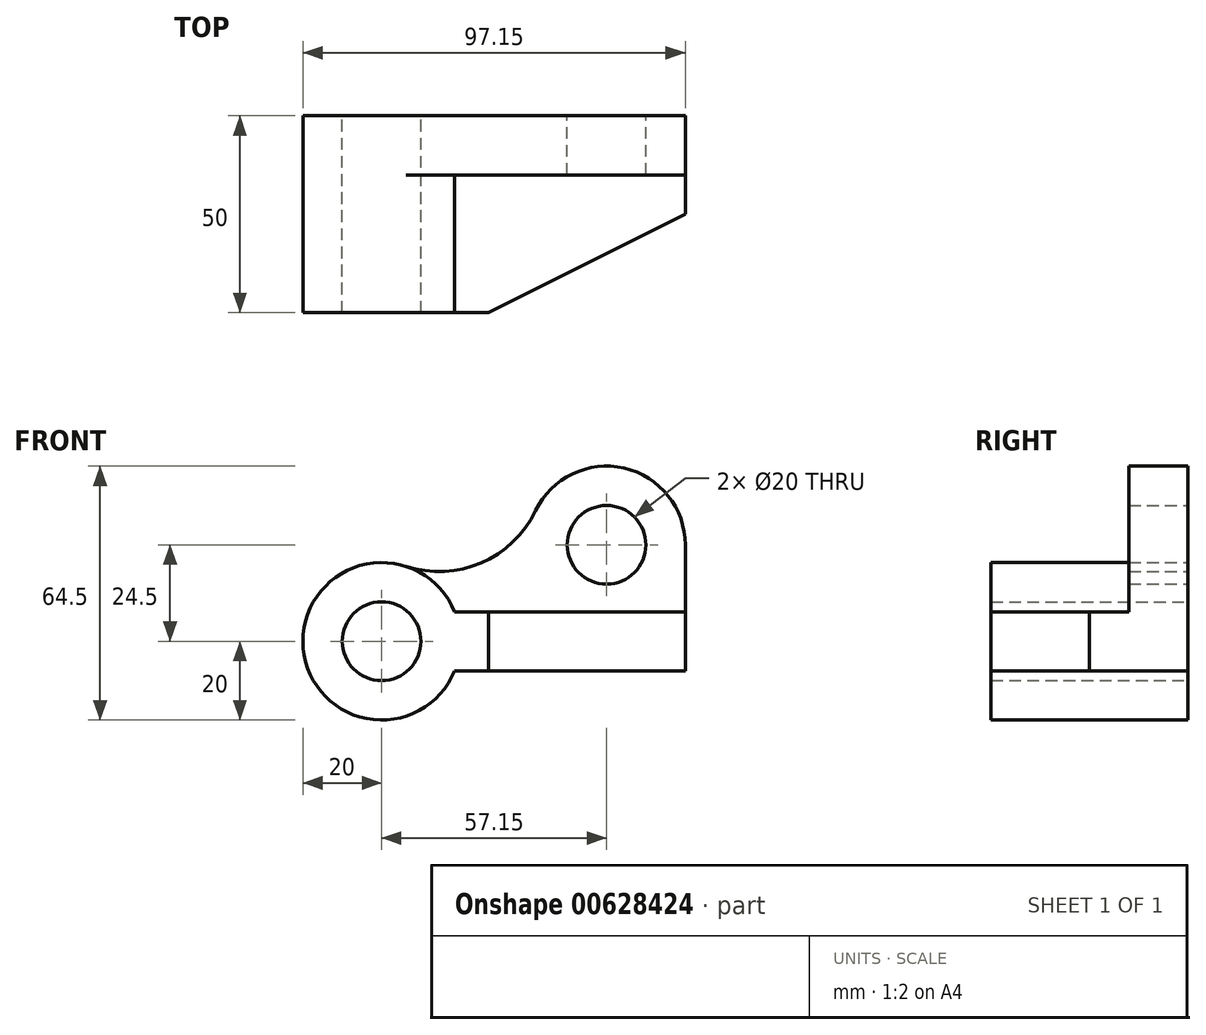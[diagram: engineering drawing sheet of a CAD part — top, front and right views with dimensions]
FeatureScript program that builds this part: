
annotation { "Feature Type Name" : "Feature", "Feature Type Description" : "" }
export const myFeature = defineFeature(function(context is Context, id is Id, definition is map)
    precondition{}
    {
        {
            var Q0;
            Q0=qCreatedBy(makeId("Front.planeOp"),FACE);
            var sketch = newSketch(context, id + "F0", { "sketchPlane" : qUnion([Q0])});
            skLineSegment(sketch, "E0", {"start": v(13.94, 14.34) * mm, "end": v(13.94, 14.34) * mm});
            skCircle(sketch, "E1", {"center": v(0, 0) * mm, "radius": 10 * mm});
            skArc(sketch, "E2", {"start": v(77.15, 24.5) * mm, "mid": v(61.6, 44) * mm, "end": v(39.13, 33.17) * mm});
            skPoint(sketch, "E3.third.point", {"position": v(14.66, 74.72) * mm});
            skCircle(sketch, "E4", {"center": v(0, 0) * mm, "radius": 20 * mm});
            skLineSegment(sketch, "E5.bottom", {"start": v(77.15, 7.5) * mm, "end": v(18.54, 7.5) * mm});
            skLineSegment(sketch, "E5.top", {"start": v(77.15, -7.5) * mm, "end": v(18.54, -7.5) * mm});
            skLineSegment(sketch, "E5.left", {"start": v(77.15, 7.5) * mm, "end": v(77.15, -7.5) * mm});
            skPoint(sketch, "E5.middle", {"position": v(45.2, 0) * mm});
            skPoint(sketch, "E6.orphan", {"position": v(13.25, 7.5) * mm});
            skPoint(sketch, "E7.orphan", {"position": v(13.25, -7.5) * mm});
            skCircle(sketch, "E8", {"center": v(57.15, 24.5) * mm, "radius": 10 * mm});
            skLineSegment(sketch, "E9", {"start": v(27.15, 7.5) * mm, "end": v(27.15, -7.5) * mm});
            skLineSegment(sketch, "E10", {"start": v(77.15, 24.5) * mm, "end": v(77.15, 7.5) * mm});
            skArc(sketch, "E11", {"start": v(6.15, 19.03) * mm, "mid": v(25.29, 19.92) * mm, "end": v(39.13, 33.17) * mm});
            skSolve(sketch);
        }
        {
            var Q0;
            Q0=makeQuery(id+"F0.imprint","IMPRINT",FACE,{"disambiguationData":[TD([[makeQuery(id+"F0.imprint","IMPRINT",EDGE,{"derivedFrom":sQuery(id+"F0.wireOp",EDGE,"E1")}),-1.0]])]});
            var Q1;
            {var subQ5=sQuery(id+"F0.wireOp",EDGE,"E9");Q1=makeQuery(id+"F0.imprint","IMPRINT",FACE,{"disambiguationData":[TD([[makeQuery(id+"F0.imprint","IMPRINT",EDGE,{"derivedFrom":subQ5}),-1.0]])]});}
            extrude(context, id + "F1", {"entities" : qUnion([Q0, Q1]), "depth" : 50 * mm, "offsetDistance" : 25 * mm});
        }
        {
            var Q0;
            Q0=makeQuery(id+"F0.imprint","IMPRINT",FACE,{"disambiguationData":[TD([[makeQuery(id+"F0.imprint","IMPRINT",EDGE,{"derivedFrom":sQuery(id+"F0.wireOp",EDGE,"E2")}),1.0]])]});
            var Q1;
            {var subQ0=sQuery(id+"F0.wireOp",EDGE,"E5.left");Q1=makeQuery(id+"F0.imprint","IMPRINT",FACE,{"disambiguationData":[TD([[makeQuery(id+"F0.imprint","IMPRINT",EDGE,{"derivedFrom":subQ0}),-1.0]])]});}
            extrude(context, id + "F2", {"entities" : qUnion([Q0, Q1]), "operationType" : NewBodyOperationType.ADD, "depth" : 15 * mm, "offsetDistance" : 25 * mm});
        }
        {
            var Q0;
            Q0=makeQuery(id+"F2.opExtrude","CAP_FACE",FACE,{"disambiguationData":[OSD([sQuery(id+"F0.wireOp",EDGE,"E2"),sQuery(id+"F0.wireOp",EDGE,"E4"),sQuery(id+"F0.wireOp",EDGE,"E5.bottom"),sQuery(id+"F0.wireOp",EDGE,"E5.top"),sQuery(id+"F0.wireOp",EDGE,"E5.left"),sQuery(id+"F0.wireOp",EDGE,"E8"),sQuery(id+"F0.wireOp",EDGE,"E9"),sQuery(id+"F0.wireOp",EDGE,"E10"),sQuery(id+"F0.wireOp",EDGE,"E11")])],"isStart":false});
            var sketch = newSketch(context, id + "F3", { "sketchPlane" : qUnion([Q0])});
            skLineSegment(sketch, "E12.bottom", {"start": v(27.15, 7.5) * mm, "end": v(77.15, 7.5) * mm});
            skLineSegment(sketch, "E12.top", {"start": v(27.15, -7.5) * mm, "end": v(77.15, -7.5) * mm});
            skLineSegment(sketch, "E12.left", {"start": v(27.15, 7.5) * mm, "end": v(27.15, -7.5) * mm});
            skLineSegment(sketch, "E12.right", {"start": v(77.15, 7.5) * mm, "end": v(77.15, -7.5) * mm});
            skSolve(sketch);
        }
        {
            var Q0;
            Q0 = qSketchRegion(id + "F3", true);
            extrude(context, id + "F4", {"entities" : qUnion([Q0]), "operationType" : NewBodyOperationType.ADD, "depth" : 35 * mm, "offsetDistance" : 25 * mm});
        }
        {
            var Q0;
            Q0=makeQuery(id+"F4.boolean.opBoolean","MERGE",FACE,{"derivedFrom":[makeQuery(id+"F1.opExtrude","SWEPT_FACE",FACE,{"disambiguationData":[OSD([sQuery(id+"F0.wireOp",EDGE,"E5.bottom")])]}),makeQuery(id+"F4.opExtrude","SWEPT_FACE",FACE,{"disambiguationData":[OSD([sQuery(id+"F3.wireOp",EDGE,"E12.bottom")])]})]});
            var sketch = newSketch(context, id + "F5", { "sketchPlane" : qUnion([Q0])});
            skLineSegment(sketch, "E13", {"start": v(27.15, -50) * mm, "end": v(77.15, -25) * mm});
            skLineSegment(sketch, "E14", {"start": v(77.15, -25) * mm, "end": v(77.15, -50) * mm});
            skLineSegment(sketch, "E15", {"start": v(77.15, -50) * mm, "end": v(27.15, -50) * mm});
            skSolve(sketch);
        }
        {
            var Q0;
            Q0 = qSketchRegion(id + "F5", true);
            var Q1;
            Q1=makeQuery(id+"F5.imprint","IMPRINT",FACE,{"disambiguationData":[TD([[makeQuery(id+"F5.imprint","IMPRINT",EDGE,{"derivedFrom":sQuery(id+"F5.wireOp",EDGE,"E13")}),-1.0]])]});
            extrude(context, id + "F6", {"entities" : qUnion([Q0, Q1]), "operationType" : NewBodyOperationType.ADD, "endBound" : BoundingType.THROUGH_ALL, "oppositeDirection" : true, "depth" : 126.8 * mm, "offsetDistance" : 25 * mm});
        }
        {
            var Q0;
            Q0=makeQuery(id+"F4.boolean.opBoolean","MERGE",FACE,{"derivedFrom":[makeQuery(id+"F1.opExtrude","SWEPT_FACE",FACE,{"disambiguationData":[OSD([sQuery(id+"F0.wireOp",EDGE,"E5.bottom")])]}),makeQuery(id+"F4.opExtrude","SWEPT_FACE",FACE,{"disambiguationData":[OSD([sQuery(id+"F3.wireOp",EDGE,"E12.bottom")])]})]});
            var sketch = newSketch(context, id + "F7", { "sketchPlane" : qUnion([Q0])});
            skLineSegment(sketch, "E16", {"start": v(27.15, -50) * mm, "end": v(77.15, -25) * mm});
            skLineSegment(sketch, "E17", {"start": v(77.15, -25) * mm, "end": v(77.15, -50) * mm});
            skLineSegment(sketch, "E18", {"start": v(77.15, -50) * mm, "end": v(27.15, -50) * mm});
            skSolve(sketch);
        }
        {
            var Q0;
            Q0 = qSketchRegion(id + "F7", true);
            extrude(context, id + "F8", {"entities" : qUnion([Q0]), "operationType" : NewBodyOperationType.REMOVE, "oppositeDirection" : true, "depth" : 257.5 * mm, "offsetDistance" : 25 * mm});
        }
    });
